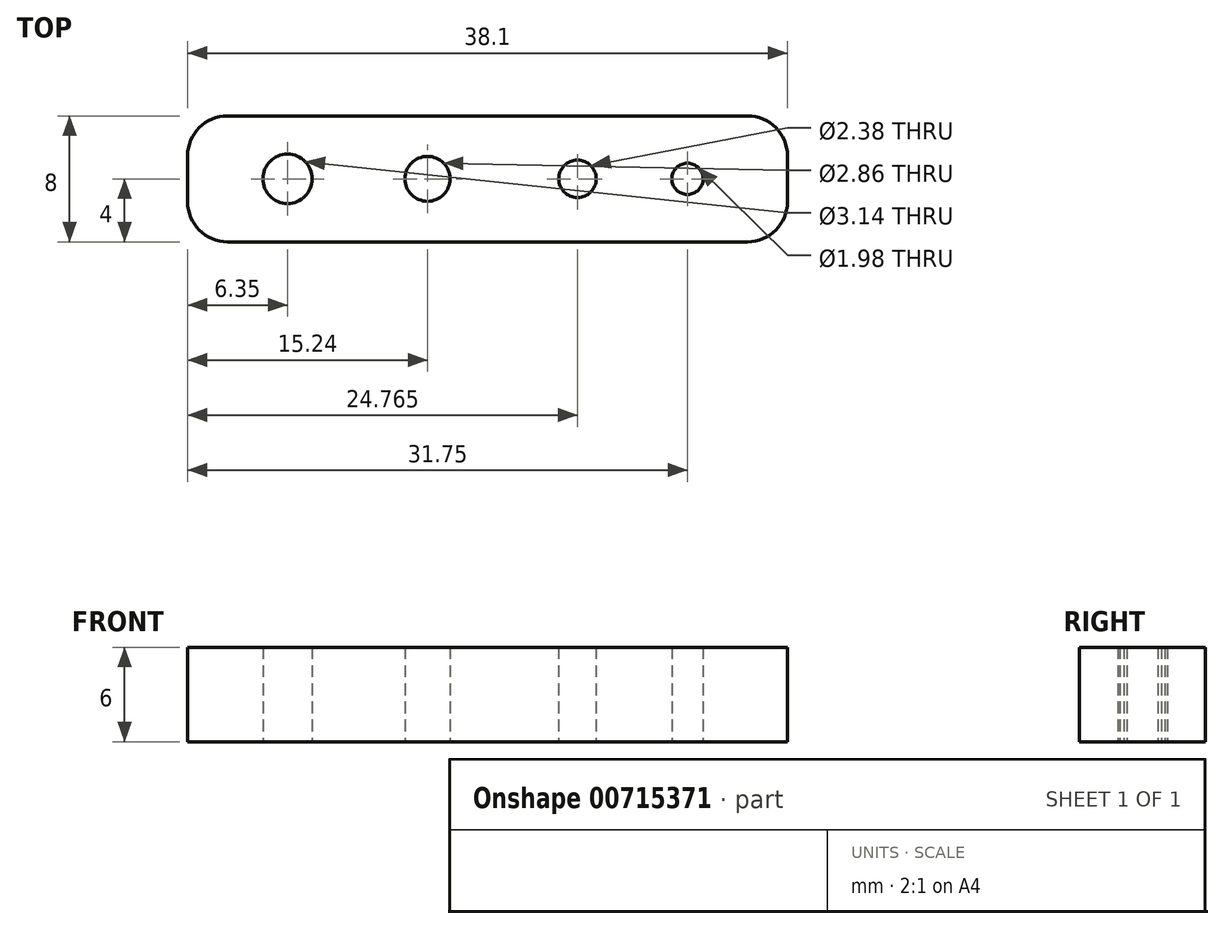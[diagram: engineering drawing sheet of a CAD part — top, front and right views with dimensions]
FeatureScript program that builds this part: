
annotation { "Feature Type Name" : "Feature", "Feature Type Description" : "" }
export const myFeature = defineFeature(function(context is Context, id is Id, definition is map)
    precondition{}
    {
        {
            var Q0;
            Q0=qCreatedBy(makeId("Top.planeOp"),FACE);
            var sketch = newSketch(context, id + "F0", { "sketchPlane" : qUnion([Q0])});
            skLineSegment(sketch, "E0.bottom", {"start": v(19.05, 4) * mm, "end": v(-19.05, 4) * mm});
            skLineSegment(sketch, "E0.top", {"start": v(19.05, -4) * mm, "end": v(-19.05, -4) * mm});
            skLineSegment(sketch, "E0.left", {"start": v(19.05, 4) * mm, "end": v(19.05, -4) * mm});
            skLineSegment(sketch, "E0.right", {"start": v(-19.05, 4) * mm, "end": v(-19.05, -4) * mm});
            skPoint(sketch, "E0.middle", {"position": v(0, 0) * mm});
            skCircle(sketch, "E1", {"center": v(-12.7, 0) * mm, "radius": 1.57 * mm});
            skCircle(sketch, "E2", {"center": v(-3.81, 0) * mm, "radius": 1.43 * mm});
            skCircle(sketch, "E3", {"center": v(5.72, 0) * mm, "radius": 1.2 * mm});
            skCircle(sketch, "E4", {"center": v(12.7, 0) * mm, "radius": 1 * mm});
            skSolve(sketch);
        }
        {
            var Q0;
            Q0=makeQuery(id+"F0.imprint","IMPRINT",FACE,{"disambiguationData":[TD([[makeQuery(id+"F0.imprint","IMPRINT",EDGE,{"derivedFrom":sQuery(id+"F0.wireOp",EDGE,"E0.bottom")}),1.0]])]});
            extrude(context, id + "F1", {"entities" : qUnion([Q0]), "depth" : 6 * mm, "offsetDistance" : 25.4 * mm});
        }
        {
            var Q0;
            Q0=makeQuery(id+"F1.opExtrude","SWEPT_EDGE",EDGE,{"disambiguationData":[OSD([sQuery(id+"F0.wireOp",EDGE,"E0.top"),sQuery(id+"F0.wireOp",EDGE,"E0.right")])]});
            var Q1;
            Q1=makeQuery(id+"F1.opExtrude","SWEPT_EDGE",EDGE,{"disambiguationData":[OSD([sQuery(id+"F0.wireOp",EDGE,"E0.top"),sQuery(id+"F0.wireOp",EDGE,"E0.left")])]});
            var Q2;
            Q2=makeQuery(id+"F1.opExtrude","SWEPT_EDGE",EDGE,{"disambiguationData":[OSD([sQuery(id+"F0.wireOp",EDGE,"E0.bottom"),sQuery(id+"F0.wireOp",EDGE,"E0.left")])]});
            var Q3;
            Q3=makeQuery(id+"F1.opExtrude","SWEPT_EDGE",EDGE,{"disambiguationData":[OSD([sQuery(id+"F0.wireOp",EDGE,"E0.bottom"),sQuery(id+"F0.wireOp",EDGE,"E0.right")])]});
            fillet(context, id + "F2", {"entities" : qUnion([Q0, Q1, Q2, Q3]), "radius" : 2.54 * mm, "tangentPropagation" : true, "allowEdgeOverflow" : false});
        }
    });
